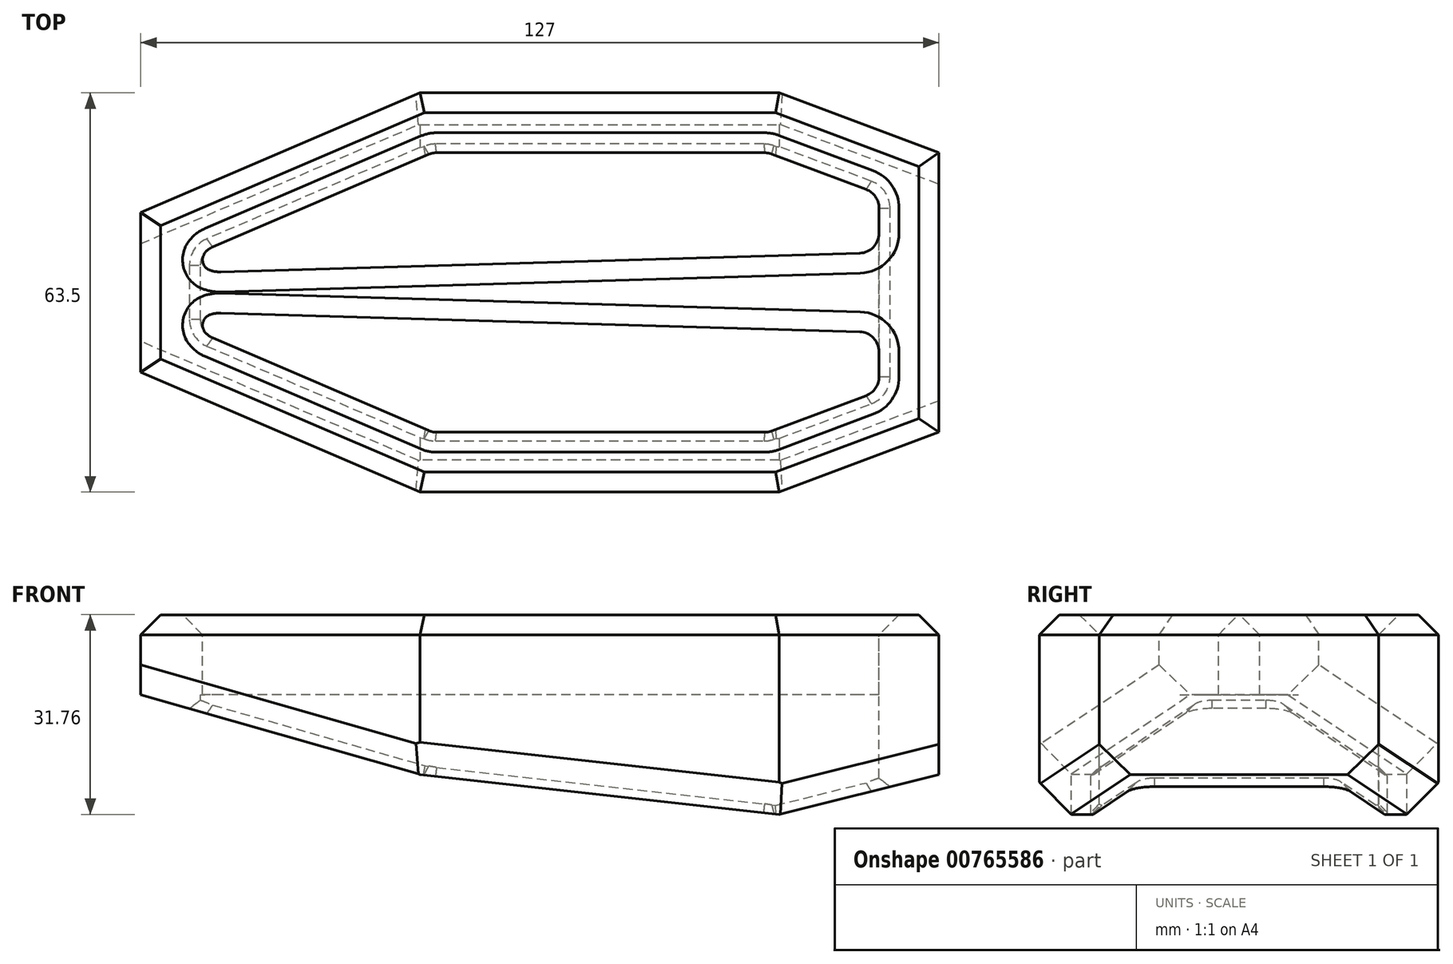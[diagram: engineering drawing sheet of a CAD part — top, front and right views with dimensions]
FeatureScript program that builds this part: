
annotation { "Feature Type Name" : "Feature", "Feature Type Description" : "" }
export const myFeature = defineFeature(function(context is Context, id is Id, definition is map)
    precondition{}
    {
        {
            var Q0;
            Q0=qCreatedBy(makeId("Front.planeOp"),FACE);
            var sketch = newSketch(context, id + "F0", { "sketchPlane" : qUnion([Q0])});
            skLineSegment(sketch, "E0.bottom", {"start": v(63.5, 34.93) * mm, "end": v(-63.5, 34.93) * mm});
            skLineSegment(sketch, "E0.top", {"start": v(63.5, -34.93) * mm, "end": v(-63.5, -34.93) * mm});
            skLineSegment(sketch, "E0.left", {"start": v(63.5, 34.93) * mm, "end": v(63.5, -34.93) * mm});
            skLineSegment(sketch, "E0.right", {"start": v(-63.5, 34.93) * mm, "end": v(-63.5, -34.93) * mm});
            skPoint(sketch, "E0.middle", {"position": v(0, 0) * mm});
            skSolve(sketch);
        }
        {
            var Q0;
            Q0=makeQuery(id+"F0.imprint","IMPRINT",FACE,{"disambiguationData":[TD([[makeQuery(id+"F0.imprint","IMPRINT",EDGE,{"derivedFrom":sQuery(id+"F0.wireOp",EDGE,"E0.bottom")}),1.0]])]});
            extrude(context, id + "F1", {"entities" : qUnion([Q0]), "endBound" : BoundingType.SYMMETRIC, "depth" : 127 * mm, "offsetDistance" : 25.4 * mm});
        }
        {
            var Q0;
            Q0=makeQuery(id+"F1.opExtrude","SWEPT_FACE",FACE,{"disambiguationData":[OSD([sQuery(id+"F0.wireOp",EDGE,"E0.bottom")])]});
            var sketch = newSketch(context, id + "F2", { "sketchPlane" : qUnion([Q0])});
            skLineSegment(sketch, "E1", {"start": v(-63.5, -12.7) * mm, "end": v(-19.05, -31.75) * mm});
            skLineSegment(sketch, "E2", {"start": v(-19.05, -31.75) * mm, "end": v(16.17, -31.75) * mm});
            skLineSegment(sketch, "E3", {"start": v(16.17, -31.75) * mm, "end": v(38.1, -31.75) * mm});
            skLineSegment(sketch, "E4", {"start": v(38.1, -31.75) * mm, "end": v(63.5, -22.22) * mm});
            skLineSegment(sketch, "E5", {"start": v(63.5, -22.22) * mm, "end": v(63.5, -63.5) * mm});
            skLineSegment(sketch, "E6", {"start": v(63.5, -63.5) * mm, "end": v(-63.5, -63.5) * mm});
            skLineSegment(sketch, "E7", {"start": v(-63.5, -63.5) * mm, "end": v(-63.5, -12.7) * mm});
            skLineSegment(sketch, "E8", {"start": v(1.92, 0) * mm, "end": v(-45.47, 0) * mm, "construction": true});
            skLineSegment(sketch, "E9.MirrorCS", {"start": v(-63.5, 12.7) * mm, "end": v(-19.05, 31.75) * mm});
            skLineSegment(sketch, "E10.MirrorCS", {"start": v(-19.05, 31.75) * mm, "end": v(16.17, 31.75) * mm});
            skLineSegment(sketch, "E11.MirrorCS", {"start": v(16.17, 31.75) * mm, "end": v(38.1, 31.75) * mm});
            skLineSegment(sketch, "E12.MirrorCS", {"start": v(38.1, 31.75) * mm, "end": v(63.5, 22.23) * mm});
            skLineSegment(sketch, "E13.MirrorCS", {"start": v(-63.5, 63.5) * mm, "end": v(-63.5, 12.7) * mm});
            skLineSegment(sketch, "E14.MirrorCS", {"start": v(63.5, 63.5) * mm, "end": v(-63.5, 63.5) * mm});
            skLineSegment(sketch, "E15.MirrorCS", {"start": v(63.5, 22.23) * mm, "end": v(63.5, 63.5) * mm});
            skSolve(sketch);
        }
        {
            var Q0;
            Q0 = qSketchRegion(id + "F2", true);
            extrude(context, id + "F3", {"entities" : qUnion([Q0]), "operationType" : NewBodyOperationType.REMOVE, "endBound" : BoundingType.THROUGH_ALL, "oppositeDirection" : true, "depth" : 25.4 * mm, "offsetDistance" : 25.4 * mm});
        }
        {
            var Q0;
            Q0=qCreatedBy(makeId("Front.planeOp"),FACE);
            var sketch = newSketch(context, id + "F4", { "sketchPlane" : qUnion([Q0])});
            skLineSegment(sketch, "E16", {"start": v(-63.5, 22.23) * mm, "end": v(-19.05, 9.53) * mm});
            skLineSegment(sketch, "E17", {"start": v(-19.05, 9.53) * mm, "end": v(38.1, 3.18) * mm});
            skLineSegment(sketch, "E18", {"start": v(38.1, 3.18) * mm, "end": v(63.5, 9.53) * mm});
            skLineSegment(sketch, "E19", {"start": v(63.5, 9.53) * mm, "end": v(63.5, -34.93) * mm});
            skLineSegment(sketch, "E20", {"start": v(63.5, -34.93) * mm, "end": v(-63.5, -34.93) * mm});
            skLineSegment(sketch, "E21", {"start": v(-63.5, -34.93) * mm, "end": v(-63.5, 22.23) * mm});
            skSolve(sketch);
        }
        {
            var Q0;
            Q0 = qSketchRegion(id + "F4", true);
            extrude(context, id + "F5", {"entities" : qUnion([Q0]), "operationType" : NewBodyOperationType.REMOVE, "endBound" : BoundingType.SYMMETRIC, "oppositeDirection" : true, "depth" : 127 * mm, "offsetDistance" : 25.4 * mm});
        }
        {
            var Q0;
            Q0=makeQuery(id+"F1.opExtrude","SWEPT_FACE",FACE,{"disambiguationData":[OSD([sQuery(id+"F0.wireOp",EDGE,"E0.bottom")])]});
            var sketch = newSketch(context, id + "F6", { "sketchPlane" : qUnion([Q0])});
            skLineSegment(sketch, "E22.0", {"start": v(-17.1, -22.22) * mm, "end": v(36.37, -22.22) * mm});
            skLineSegment(sketch, "E22.1", {"start": v(-17.1, 22.23) * mm, "end": v(36.37, 22.23) * mm});
            skLineSegment(sketch, "E22.2", {"start": v(36.37, 22.23) * mm, "end": v(53.98, 15.62) * mm});
            skLineSegment(sketch, "E22.3", {"start": v(53.98, -15.62) * mm, "end": v(53.98, -6.35) * mm});
            skLineSegment(sketch, "E22.4", {"start": v(36.37, -22.22) * mm, "end": v(53.98, -15.62) * mm});
            skLineSegment(sketch, "E23.0", {"start": v(-53.98, 6.42) * mm, "end": v(-17.1, 22.23) * mm});
            skLineSegment(sketch, "E23.1", {"start": v(-53.98, -6.42) * mm, "end": v(-53.98, -3.18) * mm});
            skLineSegment(sketch, "E23.2", {"start": v(-53.98, -6.42) * mm, "end": v(-17.1, -22.22) * mm});
            skLineSegment(sketch, "E24", {"start": v(-53.98, 3.18) * mm, "end": v(53.97, 6.35) * mm});
            skLineSegment(sketch, "E25", {"start": v(0, 0) * mm, "end": v(-53.98, 0) * mm, "construction": true});
            skLineSegment(sketch, "E26.MirrorCS", {"start": v(-53.98, -3.18) * mm, "end": v(53.98, -6.35) * mm});
            skLineSegment(sketch, "E27.trimOffspring", {"start": v(53.98, 6.35) * mm, "end": v(53.98, 15.62) * mm});
            skLineSegment(sketch, "E28.trimOffspring", {"start": v(-53.98, 3.18) * mm, "end": v(-53.98, 6.42) * mm});
            skSolve(sketch);
        }
        {
            var Q0;
            Q0 = qSketchRegion(id + "F6", true);
            extrude(context, id + "F7", {"entities" : qUnion([Q0]), "operationType" : NewBodyOperationType.REMOVE, "endBound" : BoundingType.THROUGH_ALL, "oppositeDirection" : true, "depth" : 25.4 * mm, "offsetDistance" : 25.4 * mm});
        }
        {
            var Q0;
            Q0=makeQuery(id+"F1.opExtrude","SWEPT_FACE",FACE,{"disambiguationData":[OSD([sQuery(id+"F0.wireOp",EDGE,"E0.bottom")])]});
            cPlane(context, id + "F8", {"entities" : qUnion([Q0]), "cplaneType" : CPlaneType.OFFSET, "offset" : 12.7 * mm, "oppositeDirection" : true, "width" : 152.4 * mm, "height" : 152.4 * mm});
        }
        {
            var Q0;
            Q0=qCreatedBy(id+"F8.planeOp",FACE);
            var sketch = newSketch(context, id + "F9", { "sketchPlane" : qUnion([Q0])});
            skLineSegment(sketch, "E29.0", {"start": v(-17.1, -22.22) * mm, "end": v(36.37, -22.22) * mm});
            skLineSegment(sketch, "E30.0", {"start": v(36.37, -22.22) * mm, "end": v(53.97, -15.62) * mm});
            skLineSegment(sketch, "E31.0", {"start": v(53.98, -15.62) * mm, "end": v(53.98, 15.62) * mm});
            skLineSegment(sketch, "E32.0", {"start": v(-53.98, -6.42) * mm, "end": v(-17.1, -22.22) * mm});
            skLineSegment(sketch, "E33.0", {"start": v(-53.98, -6.42) * mm, "end": v(-53.98, 6.42) * mm});
            skLineSegment(sketch, "E34.0", {"start": v(-53.98, 6.42) * mm, "end": v(-17.1, 22.23) * mm});
            skLineSegment(sketch, "E35.0", {"start": v(-17.1, 22.23) * mm, "end": v(36.37, 22.23) * mm});
            skLineSegment(sketch, "E36.0", {"start": v(36.37, 22.23) * mm, "end": v(53.98, 15.62) * mm});
            skPoint(sketch, "E37.0.start.orphan", {"position": v(53.97, 6.35) * mm});
            skPoint(sketch, "E38.0.end.orphan", {"position": v(-53.98, -3.18) * mm});
            skPoint(sketch, "E39.orphan", {"position": v(-53.98, 3.18) * mm});
            skPoint(sketch, "E40.orphan", {"position": v(53.98, -6.35) * mm});
            skSolve(sketch);
        }
        {
            var Q0;
            Q0 = qSketchRegion(id + "F9", true);
            extrude(context, id + "F10", {"entities" : qUnion([Q0]), "operationType" : NewBodyOperationType.REMOVE, "endBound" : BoundingType.THROUGH_ALL, "oppositeDirection" : true, "depth" : 25.4 * mm, "offsetDistance" : 25.4 * mm});
        }
        {
            var Q0;
            Q0=makeQuery(id+"F7.boolean.opBoolean","COPY",EDGE,{"derivedFrom":makeQuery(id+"F7.opExtrude","SWEPT_EDGE",EDGE,{"disambiguationData":[OSD([sQuery(id+"F6.wireOp",EDGE,"E23.1"),sQuery(id+"F6.wireOp",EDGE,"E23.2")])]})});
            var Q1;
            Q1=makeQuery(id+"F7.boolean.opBoolean","COPY",EDGE,{"derivedFrom":makeQuery(id+"F7.opExtrude","SWEPT_EDGE",EDGE,{"disambiguationData":[OSD([sQuery(id+"F6.wireOp",EDGE,"E23.0"),sQuery(id+"F6.wireOp",EDGE,"E28.trimOffspring")])]})});
            var Q2;
            Q2=makeQuery(id+"F7.boolean.opBoolean","COPY",EDGE,{"derivedFrom":makeQuery(id+"F7.opExtrude","SWEPT_EDGE",EDGE,{"disambiguationData":[OSD([sQuery(id+"F6.wireOp",EDGE,"E22.2"),sQuery(id+"F6.wireOp",EDGE,"E27.trimOffspring")])]})});
            var Q3;
            Q3=makeQuery(id+"F7.boolean.opBoolean","COPY",EDGE,{"derivedFrom":makeQuery(id+"F7.opExtrude","SWEPT_EDGE",EDGE,{"disambiguationData":[OSD([sQuery(id+"F6.wireOp",EDGE,"E22.3"),sQuery(id+"F6.wireOp",EDGE,"E22.4")])]})});
            var Q4;
            Q4=makeQuery(id+"F7.boolean.opBoolean","COPY",EDGE,{"derivedFrom":makeQuery(id+"F7.opExtrude","SWEPT_EDGE",EDGE,{"disambiguationData":[OSD([sQuery(id+"F6.wireOp",EDGE,"E22.1"),sQuery(id+"F6.wireOp",EDGE,"E22.2")])]})});
            var Q5;
            Q5=makeQuery(id+"F7.boolean.opBoolean","COPY",EDGE,{"derivedFrom":makeQuery(id+"F7.opExtrude","SWEPT_EDGE",EDGE,{"disambiguationData":[OSD([sQuery(id+"F6.wireOp",EDGE,"E22.1"),sQuery(id+"F6.wireOp",EDGE,"E23.0")])]})});
            var Q6;
            Q6=makeQuery(id+"F7.boolean.opBoolean","COPY",EDGE,{"derivedFrom":makeQuery(id+"F7.opExtrude","SWEPT_EDGE",EDGE,{"disambiguationData":[OSD([sQuery(id+"F6.wireOp",EDGE,"E22.0"),sQuery(id+"F6.wireOp",EDGE,"E23.2")])]})});
            var Q7;
            Q7=makeQuery(id+"F7.boolean.opBoolean","COPY",EDGE,{"derivedFrom":makeQuery(id+"F7.opExtrude","SWEPT_EDGE",EDGE,{"disambiguationData":[OSD([sQuery(id+"F6.wireOp",EDGE,"E22.0"),sQuery(id+"F6.wireOp",EDGE,"E22.4")])]})});
            var Q8;
            Q8=makeQuery(id+"F7.boolean.opBoolean","COPY",EDGE,{"derivedFrom":makeQuery(id+"F7.opExtrude","SWEPT_EDGE",EDGE,{"disambiguationData":[OSD([sQuery(id+"F6.wireOp",EDGE,"E22.3"),sQuery(id+"F6.wireOp",EDGE,"E26.MirrorCS")])]})});
            var Q9;
            Q9=makeQuery(id+"F7.boolean.opBoolean","COPY",EDGE,{"derivedFrom":makeQuery(id+"F7.opExtrude","SWEPT_EDGE",EDGE,{"disambiguationData":[OSD([sQuery(id+"F6.wireOp",EDGE,"E24"),sQuery(id+"F6.wireOp",EDGE,"E27.trimOffspring")])]})});
            fillet(context, id + "F11", {"entities" : qUnion([Q0, Q1, Q2, Q3, Q4, Q5, Q6, Q7, Q8, Q9]), "radius" : 3.17 * mm, "tangentPropagation" : true, "allowEdgeOverflow" : false});
        }
        {
            var Q0;
            Q0=makeQuery(id+"F7.boolean.opBoolean","COPY",EDGE,{"derivedFrom":makeQuery(id+"F7.opExtrude","SWEPT_EDGE",EDGE,{"disambiguationData":[OSD([sQuery(id+"F6.wireOp",EDGE,"E23.1"),sQuery(id+"F6.wireOp",EDGE,"E26.MirrorCS")])]})});
            var Q1;
            Q1=makeQuery(id+"F7.boolean.opBoolean","COPY",EDGE,{"derivedFrom":makeQuery(id+"F7.opExtrude","SWEPT_EDGE",EDGE,{"disambiguationData":[OSD([sQuery(id+"F6.wireOp",EDGE,"E24"),sQuery(id+"F6.wireOp",EDGE,"E28.trimOffspring")])]})});
            fillet(context, id + "F12", {"entities" : qUnion([Q0, Q1]), "radius" : 5.08 * mm, "tangentPropagation" : true, "allowEdgeOverflow" : false});
        }
        {
            var Q0;
            {var subQ0=sQuery(id+"F6.wireOp",EDGE,"E28.trimOffspring");Q0=makeQuery(id+"F12.opFillet","BLEND_EDGE",EDGE,{"blendedFrom":[makeQuery(id+"F7.boolean.opBoolean","COPY",EDGE,{"derivedFrom":makeQuery(id+"F7.opExtrude","SWEPT_EDGE",EDGE,{"disambiguationData":[OSD([sQuery(id+"F6.wireOp",EDGE,"E24"),subQ0])]})}),makeQuery(id+"F11.opFillet","BLEND_FACE",FACE,{"disambiguationData":[OSD([sQuery(id+"F6.wireOp",EDGE,"E23.0"),subQ0])]})],"blendedInto":[makeQuery(id+"F11.opFillet","BLEND_FACE",FACE,{"disambiguationData":[OSD([sQuery(id+"F6.wireOp",EDGE,"E23.0"),subQ0])]})]});}
            var Q1;
            {var subQ0=sQuery(id+"F6.wireOp",EDGE,"E23.1");Q1=makeQuery(id+"F12.opFillet","BLEND_EDGE",EDGE,{"blendedFrom":[makeQuery(id+"F7.boolean.opBoolean","COPY",EDGE,{"derivedFrom":makeQuery(id+"F7.opExtrude","SWEPT_EDGE",EDGE,{"disambiguationData":[OSD([subQ0,sQuery(id+"F6.wireOp",EDGE,"E26.MirrorCS")])]})}),makeQuery(id+"F11.opFillet","BLEND_FACE",FACE,{"disambiguationData":[OSD([subQ0,sQuery(id+"F6.wireOp",EDGE,"E23.2")])]})],"blendedInto":[makeQuery(id+"F11.opFillet","BLEND_FACE",FACE,{"disambiguationData":[OSD([subQ0,sQuery(id+"F6.wireOp",EDGE,"E23.2")])]})]});}
            fillet(context, id + "F13", {"entities" : qUnion([Q0, Q1]), "radius" : 1.78 * mm, "tangentPropagation" : true, "allowEdgeOverflow" : false});
        }
        {
            var Q0;
            Q0=makeQuery(id+"F1.opExtrude","SWEPT_FACE",FACE,{"disambiguationData":[OSD([sQuery(id+"F0.wireOp",EDGE,"E0.bottom")])]});
            chamfer(context, id + "F14", {"entities" : qUnion([Q0]), "width" : 3.17 * mm, "tangentPropagation" : true});
        }
        {
            var Q0;
            Q0=makeQuery(id+"F5.boolean.opBoolean","INTERSECT",EDGE,{"derivedFrom":[makeQuery(id+"F3.boolean.opBoolean","COPY",FACE,{"derivedFrom":makeQuery(id+"F3.opExtrude","SWEPT_FACE",FACE,{"disambiguationData":[OSD([sQuery(id+"F2.wireOp",EDGE,"E1")])]})}),makeQuery(id+"F5.opExtrude","SWEPT_FACE",FACE,{"disambiguationData":[OSD([sQuery(id+"F4.wireOp",EDGE,"E16")])]})]});
            var Q1;
            Q1=makeQuery(id+"F5.boolean.opBoolean","INTERSECT",EDGE,{"derivedFrom":[makeQuery(id+"F3.boolean.opBoolean","COPY",FACE,{"derivedFrom":makeQuery(id+"F3.opExtrude","SWEPT_FACE",FACE,{"disambiguationData":[OSD([sQuery(id+"F2.wireOp",EDGE,"E2"),sQuery(id+"F2.wireOp",EDGE,"E3")])]})}),makeQuery(id+"F5.opExtrude","SWEPT_FACE",FACE,{"disambiguationData":[OSD([sQuery(id+"F4.wireOp",EDGE,"E17")])]})]});
            var Q2;
            Q2=makeQuery(id+"F5.boolean.opBoolean","INTERSECT",EDGE,{"derivedFrom":[makeQuery(id+"F3.boolean.opBoolean","COPY",FACE,{"derivedFrom":makeQuery(id+"F3.opExtrude","SWEPT_FACE",FACE,{"disambiguationData":[OSD([sQuery(id+"F2.wireOp",EDGE,"E4")])]})}),makeQuery(id+"F5.opExtrude","SWEPT_FACE",FACE,{"disambiguationData":[OSD([sQuery(id+"F4.wireOp",EDGE,"E18")])]})]});
            var Q3;
            Q3=makeQuery(id+"F5.boolean.opBoolean","COPY",EDGE,{"derivedFrom":makeQuery(id+"F5.opExtrude","SWEPT_EDGE",EDGE,{"disambiguationData":[OSD([sQuery(id+"F4.wireOp",EDGE,"E16"),sQuery(id+"F4.wireOp",EDGE,"E21")])]})});
            var Q4;
            Q4=makeQuery(id+"F5.boolean.opBoolean","INTERSECT",EDGE,{"derivedFrom":[makeQuery(id+"F3.boolean.opBoolean","COPY",FACE,{"derivedFrom":makeQuery(id+"F3.opExtrude","SWEPT_FACE",FACE,{"disambiguationData":[OSD([sQuery(id+"F2.wireOp",EDGE,"E9.MirrorCS")])]})}),makeQuery(id+"F5.opExtrude","SWEPT_FACE",FACE,{"disambiguationData":[OSD([sQuery(id+"F4.wireOp",EDGE,"E16")])]})]});
            var Q5;
            Q5=makeQuery(id+"F5.boolean.opBoolean","INTERSECT",EDGE,{"derivedFrom":[makeQuery(id+"F3.boolean.opBoolean","COPY",FACE,{"derivedFrom":makeQuery(id+"F3.opExtrude","SWEPT_FACE",FACE,{"disambiguationData":[OSD([sQuery(id+"F2.wireOp",EDGE,"E10.MirrorCS"),sQuery(id+"F2.wireOp",EDGE,"E11.MirrorCS")])]})}),makeQuery(id+"F5.opExtrude","SWEPT_FACE",FACE,{"disambiguationData":[OSD([sQuery(id+"F4.wireOp",EDGE,"E17")])]})]});
            var Q6;
            Q6=makeQuery(id+"F5.boolean.opBoolean","INTERSECT",EDGE,{"derivedFrom":[makeQuery(id+"F3.boolean.opBoolean","COPY",FACE,{"derivedFrom":makeQuery(id+"F3.opExtrude","SWEPT_FACE",FACE,{"disambiguationData":[OSD([sQuery(id+"F2.wireOp",EDGE,"E12.MirrorCS")])]})}),makeQuery(id+"F5.opExtrude","SWEPT_FACE",FACE,{"disambiguationData":[OSD([sQuery(id+"F4.wireOp",EDGE,"E18")])]})]});
            chamfer(context, id + "F15", {"entities" : qUnion([Q0, Q1, Q2, Q3, Q4, Q5, Q6]), "width" : 5.08 * mm, "tangentPropagation" : true});
        }
        {
            var Q0;
            Q0=makeQuery(id+"F7.boolean.opBoolean","INTERSECT",EDGE,{"derivedFrom":[makeQuery(id+"F5.boolean.opBoolean","COPY",FACE,{"derivedFrom":makeQuery(id+"F5.opExtrude","SWEPT_FACE",FACE,{"disambiguationData":[OSD([sQuery(id+"F4.wireOp",EDGE,"E17")])]})}),makeQuery(id+"F7.opExtrude","SWEPT_FACE",FACE,{"disambiguationData":[OSD([sQuery(id+"F6.wireOp",EDGE,"E22.0")])]})]});
            var Q1;
            Q1=makeQuery(id+"F7.boolean.opBoolean","INTERSECT",EDGE,{"derivedFrom":[makeQuery(id+"F5.boolean.opBoolean","COPY",FACE,{"derivedFrom":makeQuery(id+"F5.opExtrude","SWEPT_FACE",FACE,{"disambiguationData":[OSD([sQuery(id+"F4.wireOp",EDGE,"E16")])]})}),makeQuery(id+"F7.opExtrude","SWEPT_FACE",FACE,{"disambiguationData":[OSD([sQuery(id+"F6.wireOp",EDGE,"E23.2")])]})]});
            var Q2;
            Q2=makeQuery(id+"F7.boolean.opBoolean","INTERSECT",EDGE,{"derivedFrom":[makeQuery(id+"F5.boolean.opBoolean","COPY",FACE,{"derivedFrom":makeQuery(id+"F5.opExtrude","SWEPT_FACE",FACE,{"disambiguationData":[OSD([sQuery(id+"F4.wireOp",EDGE,"E18")])]})}),makeQuery(id+"F7.opExtrude","SWEPT_FACE",FACE,{"disambiguationData":[OSD([sQuery(id+"F6.wireOp",EDGE,"E22.4")])]})]});
            var Q3;
            Q3=makeQuery(id+"F7.boolean.opBoolean","INTERSECT",EDGE,{"derivedFrom":[makeQuery(id+"F5.boolean.opBoolean","COPY",FACE,{"derivedFrom":makeQuery(id+"F5.opExtrude","SWEPT_FACE",FACE,{"disambiguationData":[OSD([sQuery(id+"F4.wireOp",EDGE,"E17")])]})}),makeQuery(id+"F7.opExtrude","SWEPT_FACE",FACE,{"disambiguationData":[OSD([sQuery(id+"F6.wireOp",EDGE,"E22.4")])]})]});
            var Q4;
            {var subQ0=sQuery(id+"F6.wireOp",EDGE,"E22.0");var subQ1=sQuery(id+"F6.wireOp",EDGE,"E22.4");Q4=makeQuery(id+"F11.opFillet","BLEND_EDGE",EDGE,{"blendedFrom":[makeQuery(id+"F7.boolean.opBoolean","COPY",EDGE,{"derivedFrom":makeQuery(id+"F7.opExtrude","SWEPT_EDGE",EDGE,{"disambiguationData":[OSD([subQ0,subQ1])]})}),makeQuery(id+"F7.boolean.opBoolean","SPLIT",FACE,{"disambiguationData":[TD([makeQuery(id+"F3.boolean.opBoolean","COPY",FACE,{"derivedFrom":makeQuery(id+"F3.opExtrude","SWEPT_FACE",FACE,{"disambiguationData":[OSD([sQuery(id+"F2.wireOp",EDGE,"E1")])]})})])],"derivedFrom":makeQuery(id+"F5.boolean.opBoolean","COPY",FACE,{"derivedFrom":makeQuery(id+"F5.opExtrude","SWEPT_FACE",FACE,{"disambiguationData":[OSD([sQuery(id+"F4.wireOp",EDGE,"E17")])]})})})],"blendedInto":[makeQuery(id+"F7.boolean.opBoolean","SPLIT",FACE,{"disambiguationData":[TD([makeQuery(id+"F3.boolean.opBoolean","COPY",FACE,{"derivedFrom":makeQuery(id+"F3.opExtrude","SWEPT_FACE",FACE,{"disambiguationData":[OSD([sQuery(id+"F2.wireOp",EDGE,"E1")])]})})])],"derivedFrom":makeQuery(id+"F5.boolean.opBoolean","COPY",FACE,{"derivedFrom":makeQuery(id+"F5.opExtrude","SWEPT_FACE",FACE,{"disambiguationData":[OSD([sQuery(id+"F4.wireOp",EDGE,"E17")])]})})})]});}
            var Q5;
            Q5=makeQuery(id+"F11.opFillet","BLEND_EDGE",EDGE,{"blendedFrom":[makeQuery(id+"F7.boolean.opBoolean","COPY",EDGE,{"derivedFrom":makeQuery(id+"F7.opExtrude","SWEPT_EDGE",EDGE,{"disambiguationData":[OSD([sQuery(id+"F6.wireOp",EDGE,"E22.3"),sQuery(id+"F6.wireOp",EDGE,"E22.4")])]})}),makeQuery(id+"F5.boolean.opBoolean","COPY",FACE,{"derivedFrom":makeQuery(id+"F5.opExtrude","SWEPT_FACE",FACE,{"disambiguationData":[OSD([sQuery(id+"F4.wireOp",EDGE,"E18")])]})})],"blendedInto":[makeQuery(id+"F5.boolean.opBoolean","COPY",FACE,{"derivedFrom":makeQuery(id+"F5.opExtrude","SWEPT_FACE",FACE,{"disambiguationData":[OSD([sQuery(id+"F4.wireOp",EDGE,"E18")])]})})]});
            var Q6;
            {var subQ0=makeQuery(id+"F5.boolean.opBoolean","COPY",FACE,{"derivedFrom":makeQuery(id+"F5.opExtrude","SWEPT_FACE",FACE,{"disambiguationData":[OSD([sQuery(id+"F4.wireOp",EDGE,"E18")])]})});Q6=makeQuery(id+"F10.boolean.opBoolean","MERGE",EDGE,{"derivedFrom":[makeQuery(id+"F7.boolean.opBoolean","INTERSECT",EDGE,{"derivedFrom":[subQ0,makeQuery(id+"F7.opExtrude","SWEPT_FACE",FACE,{"disambiguationData":[OSD([sQuery(id+"F6.wireOp",EDGE,"E22.3")])]})]}),makeQuery(id+"F7.boolean.opBoolean","INTERSECT",EDGE,{"derivedFrom":[subQ0,makeQuery(id+"F7.opExtrude","SWEPT_FACE",FACE,{"disambiguationData":[OSD([sQuery(id+"F6.wireOp",EDGE,"E27.trimOffspring")])]})]})]});}
            var Q7;
            Q7=makeQuery(id+"F11.opFillet","BLEND_EDGE",EDGE,{"blendedFrom":[makeQuery(id+"F7.boolean.opBoolean","COPY",EDGE,{"derivedFrom":makeQuery(id+"F7.opExtrude","SWEPT_EDGE",EDGE,{"disambiguationData":[OSD([sQuery(id+"F6.wireOp",EDGE,"E22.2"),sQuery(id+"F6.wireOp",EDGE,"E27.trimOffspring")])]})}),makeQuery(id+"F5.boolean.opBoolean","COPY",FACE,{"derivedFrom":makeQuery(id+"F5.opExtrude","SWEPT_FACE",FACE,{"disambiguationData":[OSD([sQuery(id+"F4.wireOp",EDGE,"E18")])]})})],"blendedInto":[makeQuery(id+"F5.boolean.opBoolean","COPY",FACE,{"derivedFrom":makeQuery(id+"F5.opExtrude","SWEPT_FACE",FACE,{"disambiguationData":[OSD([sQuery(id+"F4.wireOp",EDGE,"E18")])]})})]});
            var Q8;
            Q8=makeQuery(id+"F7.boolean.opBoolean","INTERSECT",EDGE,{"derivedFrom":[makeQuery(id+"F5.boolean.opBoolean","COPY",FACE,{"derivedFrom":makeQuery(id+"F5.opExtrude","SWEPT_FACE",FACE,{"disambiguationData":[OSD([sQuery(id+"F4.wireOp",EDGE,"E18")])]})}),makeQuery(id+"F7.opExtrude","SWEPT_FACE",FACE,{"disambiguationData":[OSD([sQuery(id+"F6.wireOp",EDGE,"E22.2")])]})]});
            var Q9;
            Q9=makeQuery(id+"F7.boolean.opBoolean","INTERSECT",EDGE,{"derivedFrom":[makeQuery(id+"F5.boolean.opBoolean","COPY",FACE,{"derivedFrom":makeQuery(id+"F5.opExtrude","SWEPT_FACE",FACE,{"disambiguationData":[OSD([sQuery(id+"F4.wireOp",EDGE,"E17")])]})}),makeQuery(id+"F7.opExtrude","SWEPT_FACE",FACE,{"disambiguationData":[OSD([sQuery(id+"F6.wireOp",EDGE,"E22.2")])]})]});
            var Q10;
            {var subQ0=sQuery(id+"F6.wireOp",EDGE,"E22.1");var subQ1=sQuery(id+"F6.wireOp",EDGE,"E22.2");Q10=makeQuery(id+"F11.opFillet","BLEND_EDGE",EDGE,{"blendedFrom":[makeQuery(id+"F7.boolean.opBoolean","COPY",EDGE,{"derivedFrom":makeQuery(id+"F7.opExtrude","SWEPT_EDGE",EDGE,{"disambiguationData":[OSD([subQ0,subQ1])]})}),makeQuery(id+"F7.boolean.opBoolean","SPLIT",FACE,{"disambiguationData":[TD([makeQuery(id+"F3.boolean.opBoolean","COPY",FACE,{"derivedFrom":makeQuery(id+"F3.opExtrude","SWEPT_FACE",FACE,{"disambiguationData":[OSD([sQuery(id+"F2.wireOp",EDGE,"E9.MirrorCS")])]})})])],"derivedFrom":makeQuery(id+"F5.boolean.opBoolean","COPY",FACE,{"derivedFrom":makeQuery(id+"F5.opExtrude","SWEPT_FACE",FACE,{"disambiguationData":[OSD([sQuery(id+"F4.wireOp",EDGE,"E17")])]})})})],"blendedInto":[makeQuery(id+"F7.boolean.opBoolean","SPLIT",FACE,{"disambiguationData":[TD([makeQuery(id+"F3.boolean.opBoolean","COPY",FACE,{"derivedFrom":makeQuery(id+"F3.opExtrude","SWEPT_FACE",FACE,{"disambiguationData":[OSD([sQuery(id+"F2.wireOp",EDGE,"E9.MirrorCS")])]})})])],"derivedFrom":makeQuery(id+"F5.boolean.opBoolean","COPY",FACE,{"derivedFrom":makeQuery(id+"F5.opExtrude","SWEPT_FACE",FACE,{"disambiguationData":[OSD([sQuery(id+"F4.wireOp",EDGE,"E17")])]})})})]});}
            var Q11;
            Q11=makeQuery(id+"F7.boolean.opBoolean","INTERSECT",EDGE,{"derivedFrom":[makeQuery(id+"F5.boolean.opBoolean","COPY",FACE,{"derivedFrom":makeQuery(id+"F5.opExtrude","SWEPT_FACE",FACE,{"disambiguationData":[OSD([sQuery(id+"F4.wireOp",EDGE,"E17")])]})}),makeQuery(id+"F7.opExtrude","SWEPT_FACE",FACE,{"disambiguationData":[OSD([sQuery(id+"F6.wireOp",EDGE,"E22.1")])]})]});
            var Q12;
            Q12=makeQuery(id+"F7.boolean.opBoolean","INTERSECT",EDGE,{"derivedFrom":[makeQuery(id+"F5.boolean.opBoolean","COPY",FACE,{"derivedFrom":makeQuery(id+"F5.opExtrude","SWEPT_FACE",FACE,{"disambiguationData":[OSD([sQuery(id+"F4.wireOp",EDGE,"E16")])]})}),makeQuery(id+"F7.opExtrude","SWEPT_FACE",FACE,{"disambiguationData":[OSD([sQuery(id+"F6.wireOp",EDGE,"E23.0")])]})]});
            var Q13;
            {var subQ0=sQuery(id+"F6.wireOp",EDGE,"E23.0");var subQ1=sQuery(id+"F6.wireOp",EDGE,"E22.1");Q13=makeQuery(id+"F11.opFillet","BLEND_EDGE",EDGE,{"blendedFrom":[makeQuery(id+"F7.boolean.opBoolean","COPY",EDGE,{"derivedFrom":makeQuery(id+"F7.opExtrude","SWEPT_EDGE",EDGE,{"disambiguationData":[OSD([subQ1,subQ0])]})}),makeQuery(id+"F7.boolean.opBoolean","SPLIT",FACE,{"disambiguationData":[TD([makeQuery(id+"F3.boolean.opBoolean","COPY",FACE,{"derivedFrom":makeQuery(id+"F3.opExtrude","SWEPT_FACE",FACE,{"disambiguationData":[OSD([sQuery(id+"F2.wireOp",EDGE,"E9.MirrorCS")])]})})])],"derivedFrom":makeQuery(id+"F5.boolean.opBoolean","COPY",FACE,{"derivedFrom":makeQuery(id+"F5.opExtrude","SWEPT_FACE",FACE,{"disambiguationData":[OSD([sQuery(id+"F4.wireOp",EDGE,"E17")])]})})})],"blendedInto":[makeQuery(id+"F7.boolean.opBoolean","SPLIT",FACE,{"disambiguationData":[TD([makeQuery(id+"F3.boolean.opBoolean","COPY",FACE,{"derivedFrom":makeQuery(id+"F3.opExtrude","SWEPT_FACE",FACE,{"disambiguationData":[OSD([sQuery(id+"F2.wireOp",EDGE,"E9.MirrorCS")])]})})])],"derivedFrom":makeQuery(id+"F5.boolean.opBoolean","COPY",FACE,{"derivedFrom":makeQuery(id+"F5.opExtrude","SWEPT_FACE",FACE,{"disambiguationData":[OSD([sQuery(id+"F4.wireOp",EDGE,"E17")])]})})})]});}
            var Q14;
            Q14=makeQuery(id+"F7.boolean.opBoolean","INTERSECT",EDGE,{"derivedFrom":[makeQuery(id+"F5.boolean.opBoolean","COPY",FACE,{"derivedFrom":makeQuery(id+"F5.opExtrude","SWEPT_FACE",FACE,{"disambiguationData":[OSD([sQuery(id+"F4.wireOp",EDGE,"E17")])]})}),makeQuery(id+"F7.opExtrude","SWEPT_FACE",FACE,{"disambiguationData":[OSD([sQuery(id+"F6.wireOp",EDGE,"E23.0")])]})]});
            var Q15;
            Q15=makeQuery(id+"F11.opFillet","BLEND_EDGE",EDGE,{"blendedFrom":[makeQuery(id+"F7.boolean.opBoolean","COPY",EDGE,{"derivedFrom":makeQuery(id+"F7.opExtrude","SWEPT_EDGE",EDGE,{"disambiguationData":[OSD([sQuery(id+"F6.wireOp",EDGE,"E23.0"),sQuery(id+"F6.wireOp",EDGE,"E28.trimOffspring")])]})}),makeQuery(id+"F5.boolean.opBoolean","COPY",FACE,{"derivedFrom":makeQuery(id+"F5.opExtrude","SWEPT_FACE",FACE,{"disambiguationData":[OSD([sQuery(id+"F4.wireOp",EDGE,"E16")])]})})],"blendedInto":[makeQuery(id+"F5.boolean.opBoolean","COPY",FACE,{"derivedFrom":makeQuery(id+"F5.opExtrude","SWEPT_FACE",FACE,{"disambiguationData":[OSD([sQuery(id+"F4.wireOp",EDGE,"E16")])]})})]});
            var Q16;
            {var subQ0=makeQuery(id+"F5.boolean.opBoolean","COPY",FACE,{"derivedFrom":makeQuery(id+"F5.opExtrude","SWEPT_FACE",FACE,{"disambiguationData":[OSD([sQuery(id+"F4.wireOp",EDGE,"E16")])]})});Q16=makeQuery(id+"F10.boolean.opBoolean","MERGE",EDGE,{"derivedFrom":[makeQuery(id+"F7.boolean.opBoolean","INTERSECT",EDGE,{"derivedFrom":[subQ0,makeQuery(id+"F7.opExtrude","SWEPT_FACE",FACE,{"disambiguationData":[OSD([sQuery(id+"F6.wireOp",EDGE,"E23.1")])]})]}),makeQuery(id+"F7.boolean.opBoolean","INTERSECT",EDGE,{"derivedFrom":[subQ0,makeQuery(id+"F7.opExtrude","SWEPT_FACE",FACE,{"disambiguationData":[OSD([sQuery(id+"F6.wireOp",EDGE,"E28.trimOffspring")])]})]})]});}
            var Q17;
            Q17=makeQuery(id+"F11.opFillet","BLEND_EDGE",EDGE,{"blendedFrom":[makeQuery(id+"F7.boolean.opBoolean","COPY",EDGE,{"derivedFrom":makeQuery(id+"F7.opExtrude","SWEPT_EDGE",EDGE,{"disambiguationData":[OSD([sQuery(id+"F6.wireOp",EDGE,"E23.1"),sQuery(id+"F6.wireOp",EDGE,"E23.2")])]})}),makeQuery(id+"F5.boolean.opBoolean","COPY",FACE,{"derivedFrom":makeQuery(id+"F5.opExtrude","SWEPT_FACE",FACE,{"disambiguationData":[OSD([sQuery(id+"F4.wireOp",EDGE,"E16")])]})})],"blendedInto":[makeQuery(id+"F5.boolean.opBoolean","COPY",FACE,{"derivedFrom":makeQuery(id+"F5.opExtrude","SWEPT_FACE",FACE,{"disambiguationData":[OSD([sQuery(id+"F4.wireOp",EDGE,"E16")])]})})]});
            var Q18;
            {var subQ0=sQuery(id+"F6.wireOp",EDGE,"E22.0");var subQ1=sQuery(id+"F6.wireOp",EDGE,"E23.2");Q18=makeQuery(id+"F11.opFillet","BLEND_EDGE",EDGE,{"blendedFrom":[makeQuery(id+"F7.boolean.opBoolean","COPY",EDGE,{"derivedFrom":makeQuery(id+"F7.opExtrude","SWEPT_EDGE",EDGE,{"disambiguationData":[OSD([subQ0,subQ1])]})}),makeQuery(id+"F7.boolean.opBoolean","SPLIT",FACE,{"disambiguationData":[TD([makeQuery(id+"F3.boolean.opBoolean","COPY",FACE,{"derivedFrom":makeQuery(id+"F3.opExtrude","SWEPT_FACE",FACE,{"disambiguationData":[OSD([sQuery(id+"F2.wireOp",EDGE,"E1")])]})})])],"derivedFrom":makeQuery(id+"F5.boolean.opBoolean","COPY",FACE,{"derivedFrom":makeQuery(id+"F5.opExtrude","SWEPT_FACE",FACE,{"disambiguationData":[OSD([sQuery(id+"F4.wireOp",EDGE,"E17")])]})})})],"blendedInto":[makeQuery(id+"F7.boolean.opBoolean","SPLIT",FACE,{"disambiguationData":[TD([makeQuery(id+"F3.boolean.opBoolean","COPY",FACE,{"derivedFrom":makeQuery(id+"F3.opExtrude","SWEPT_FACE",FACE,{"disambiguationData":[OSD([sQuery(id+"F2.wireOp",EDGE,"E1")])]})})])],"derivedFrom":makeQuery(id+"F5.boolean.opBoolean","COPY",FACE,{"derivedFrom":makeQuery(id+"F5.opExtrude","SWEPT_FACE",FACE,{"disambiguationData":[OSD([sQuery(id+"F4.wireOp",EDGE,"E17")])]})})})]});}
            var Q19;
            Q19=makeQuery(id+"F7.boolean.opBoolean","INTERSECT",EDGE,{"derivedFrom":[makeQuery(id+"F5.boolean.opBoolean","COPY",FACE,{"derivedFrom":makeQuery(id+"F5.opExtrude","SWEPT_FACE",FACE,{"disambiguationData":[OSD([sQuery(id+"F4.wireOp",EDGE,"E17")])]})}),makeQuery(id+"F7.opExtrude","SWEPT_FACE",FACE,{"disambiguationData":[OSD([sQuery(id+"F6.wireOp",EDGE,"E23.2")])]})]});
            chamfer(context, id + "F16", {"entities" : qUnion([Q0, Q1, Q2, Q3, Q4, Q5, Q6, Q7, Q8, Q9, Q10, Q11, Q12, Q13, Q14, Q15, Q16, Q17, Q18, Q19]), "width" : 1.4 * mm, "tangentPropagation" : true});
        }
    });
